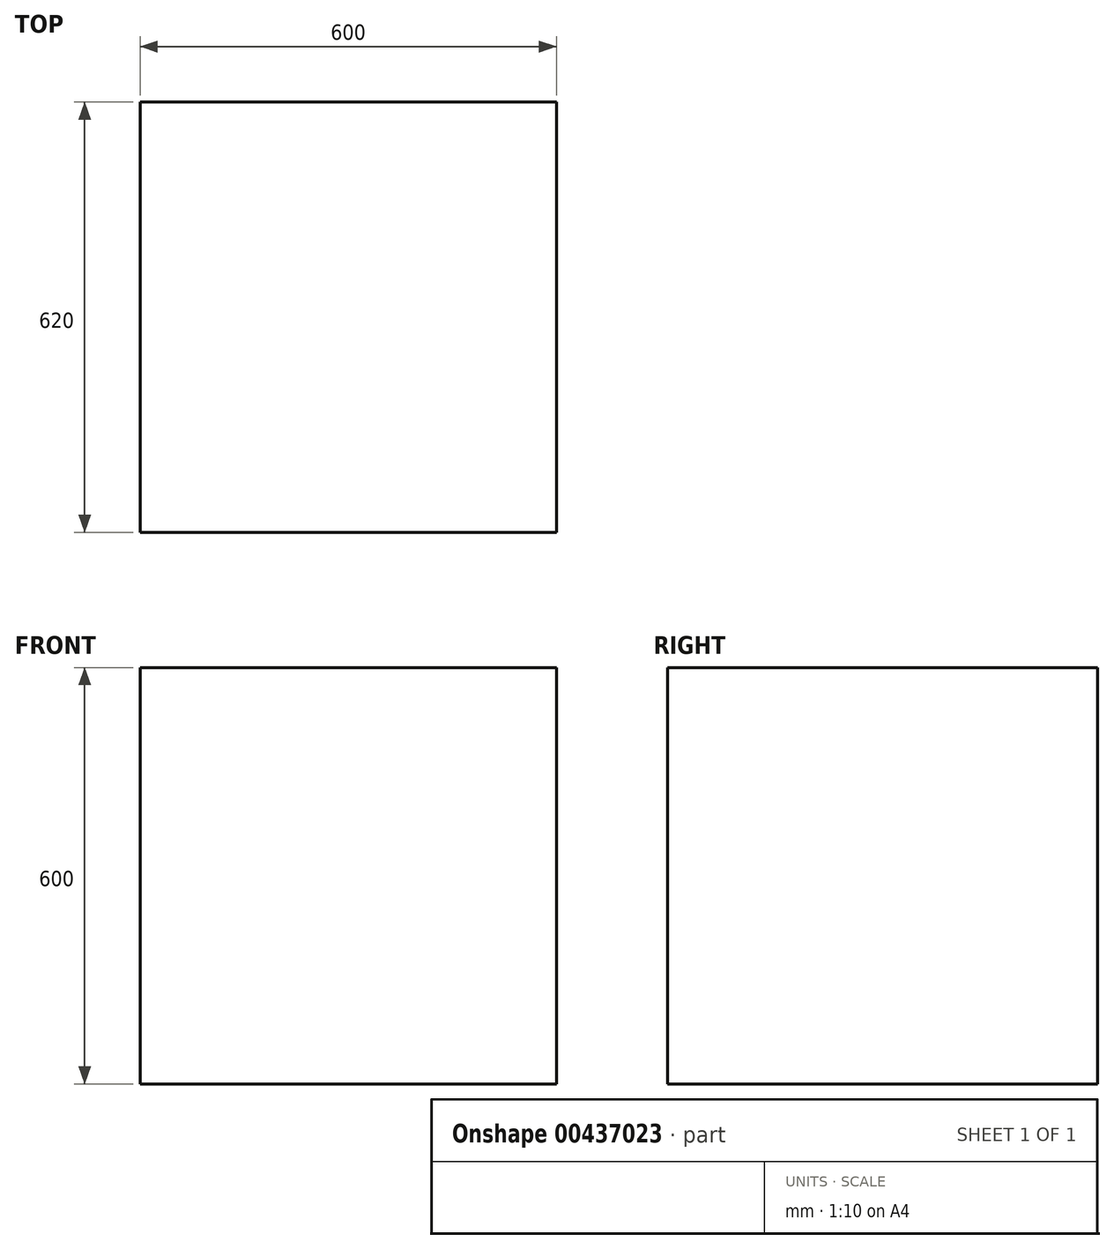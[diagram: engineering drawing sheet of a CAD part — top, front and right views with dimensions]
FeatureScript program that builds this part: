
annotation { "Feature Type Name" : "Feature", "Feature Type Description" : "" }
export const myFeature = defineFeature(function(context is Context, id is Id, definition is map)
    precondition{}
    {
        {
            var Q0;
            Q0=qCreatedBy(makeId("Right.planeOp"),FACE);
            var sketch = newSketch(context, id + "F0", { "sketchPlane" : qUnion([Q0])});
            skLineSegment(sketch, "E0.bottom", {"start": v(0, 0) * mm, "end": v(-620, 0) * mm});
            skLineSegment(sketch, "E0.top", {"start": v(0, 600) * mm, "end": v(-620, 600) * mm});
            skLineSegment(sketch, "E0.left", {"start": v(0, 0) * mm, "end": v(0, 600) * mm});
            skLineSegment(sketch, "E0.right", {"start": v(-620, 0) * mm, "end": v(-620, 600) * mm});
            skSolve(sketch);
        }
        {
            var Q0;
            Q0 = qSketchRegion(id + "F0", true);
            extrude(context, id + "F1", {"entities" : qUnion([Q0]), "depth" : 600 * mm});
        }
    });
